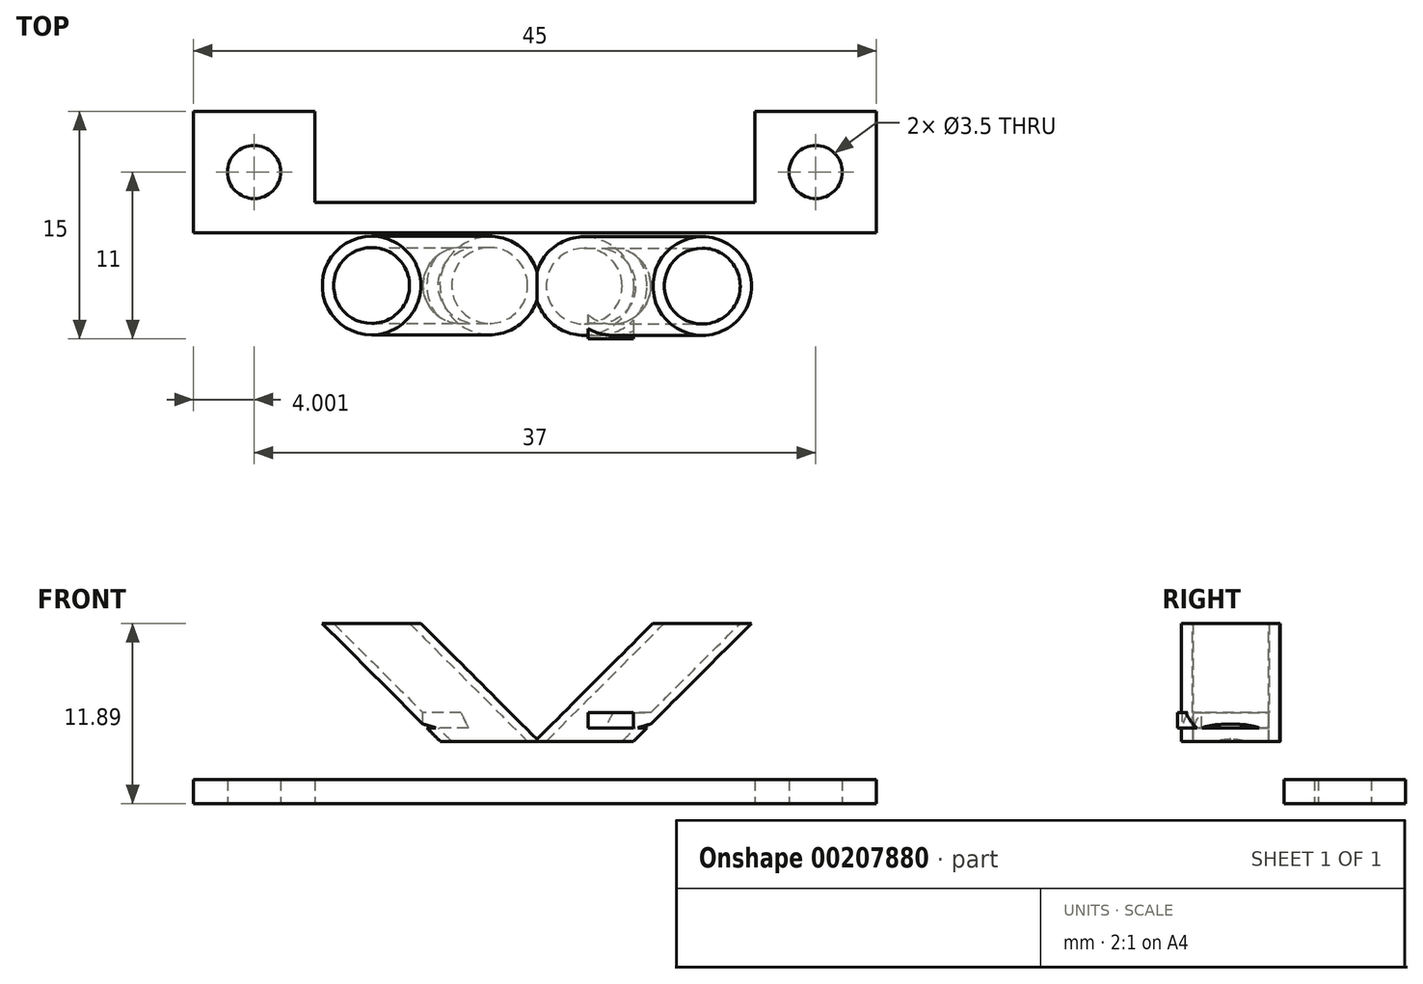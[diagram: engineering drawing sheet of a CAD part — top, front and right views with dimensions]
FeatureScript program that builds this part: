
annotation { "Feature Type Name" : "Feature", "Feature Type Description" : "" }
export const myFeature = defineFeature(function(context is Context, id is Id, definition is map)
    precondition{}
    {
        {
            var Q0;
            Q0=qCreatedBy(makeId("Top.planeOp"),FACE);
            var sketch = newSketch(context, id + "F0", { "sketchPlane" : qUnion([Q0])});
            skLineSegment(sketch, "E0.bottom", {"start": v(-20.07, 6) * mm, "end": v(-12.07, 6) * mm});
            skLineSegment(sketch, "E0.top", {"start": v(-20.07, -2) * mm, "end": v(-12.07, -2) * mm});
            skLineSegment(sketch, "E0.left", {"start": v(-20.07, 6) * mm, "end": v(-20.07, -2) * mm});
            skLineSegment(sketch, "E0.right", {"start": v(-12.07, 6) * mm, "end": v(-12.07, -2) * mm});
            skLineSegment(sketch, "E1.bottom", {"start": v(16.93, 6) * mm, "end": v(24.93, 6) * mm});
            skLineSegment(sketch, "E1.top", {"start": v(16.93, -2) * mm, "end": v(24.93, -2) * mm});
            skLineSegment(sketch, "E1.left", {"start": v(16.93, 6) * mm, "end": v(16.93, -2) * mm});
            skLineSegment(sketch, "E1.right", {"start": v(24.93, 6) * mm, "end": v(24.93, -2) * mm});
            skLineSegment(sketch, "E2.bottom", {"start": v(-12.07, 0) * mm, "end": v(16.93, 0) * mm});
            skLineSegment(sketch, "E2.top", {"start": v(-12.07, -2) * mm, "end": v(16.93, -2) * mm});
            skLineSegment(sketch, "E2.left", {"start": v(-12.07, 0) * mm, "end": v(-12.07, -2) * mm});
            skLineSegment(sketch, "E2.right", {"start": v(16.93, 0) * mm, "end": v(16.93, -2) * mm});
            skLineSegment(sketch, "E3.top", {"start": v(-12.07, -9) * mm, "end": v(16.93, -9) * mm});
            skLineSegment(sketch, "E3.left", {"start": v(-12.07, -2) * mm, "end": v(-12.07, -9) * mm});
            skLineSegment(sketch, "E3.right", {"start": v(16.93, -2) * mm, "end": v(16.93, -9) * mm});
            skLineSegment(sketch, "E4.bottom", {"start": v(-4.07, -9) * mm, "end": v(-1.07, -9) * mm});
            skLineSegment(sketch, "E4.top", {"start": v(-4.07, -5) * mm, "end": v(-1.07, -5) * mm});
            skLineSegment(sketch, "E4.left", {"start": v(-4.07, -9) * mm, "end": v(-4.07, -5) * mm});
            skLineSegment(sketch, "E4.right", {"start": v(-1.07, -9) * mm, "end": v(-1.07, -5) * mm});
            skLineSegment(sketch, "E5.bottom", {"start": v(5.93, -5) * mm, "end": v(8.93, -5) * mm});
            skLineSegment(sketch, "E5.top", {"start": v(5.93, -9) * mm, "end": v(8.93, -9) * mm});
            skLineSegment(sketch, "E5.left", {"start": v(5.93, -5) * mm, "end": v(5.93, -9) * mm});
            skLineSegment(sketch, "E5.right", {"start": v(8.93, -5) * mm, "end": v(8.93, -9) * mm});
            skCircle(sketch, "E6", {"center": v(20.93, 2) * mm, "radius": 1.75 * mm});
            skPoint(sketch, "E6.centerSnap0", {"position": v(16.93, 2) * mm});
            skPoint(sketch, "E6.centerSnap1", {"position": v(20.93, 6) * mm});
            skCircle(sketch, "E7", {"center": v(-16.07, 2) * mm, "radius": 1.75 * mm});
            skPoint(sketch, "E7.centerSnap0", {"position": v(-20.07, 2) * mm});
            skPoint(sketch, "E7.centerSnap1", {"position": v(-16.07, 6) * mm});
            skSolve(sketch);
        }
        {
            var Q0;
            Q0=makeQuery(id+"F0.imprint","IMPRINT",FACE,{"disambiguationData":[TD([[makeQuery(id+"F0.imprint","IMPRINT",EDGE,{"derivedFrom":sQuery(id+"F0.wireOp",EDGE,"E0.bottom")}),-1.0]])]});
            var Q1;
            Q1=makeQuery(id+"F0.imprint","IMPRINT",FACE,{"disambiguationData":[TD([[makeQuery(id+"F0.imprint","IMPRINT",EDGE,{"derivedFrom":sQuery(id+"F0.wireOp",EDGE,"E2.bottom")}),-1.0]])]});
            var Q2;
            Q2=makeQuery(id+"F0.imprint","IMPRINT",FACE,{"disambiguationData":[TD([[makeQuery(id+"F0.imprint","IMPRINT",EDGE,{"derivedFrom":sQuery(id+"F0.wireOp",EDGE,"E1.bottom")}),-1.0]])]});
            extrude(context, id + "F1", {"entities" : qUnion([Q0, Q1, Q2]), "depth" : 1.6 * mm});
        }
        {
            var Q0;
            Q0=makeQuery(id+"F0.imprint","IMPRINT",FACE,{"disambiguationData":[TD([[makeQuery(id+"F0.imprint","IMPRINT",EDGE,{"derivedFrom":sQuery(id+"F0.wireOp",EDGE,"E2.top")}),-1.0]])]});
            var Q1;
            Q1=makeQuery(id+"F0.imprint","IMPRINT",FACE,{"disambiguationData":[TD([[makeQuery(id+"F0.imprint","IMPRINT",EDGE,{"derivedFrom":sQuery(id+"F0.wireOp",EDGE,"E4.bottom")}),1.0]])]});
            var Q2;
            Q2=makeQuery(id+"F0.imprint","IMPRINT",FACE,{"disambiguationData":[TD([[makeQuery(id+"F0.imprint","IMPRINT",EDGE,{"derivedFrom":sQuery(id+"F0.wireOp",EDGE,"E5.bottom")}),-1.0]])]});
            extrude(context, id + "F2", {"entities" : qUnion([Q0, Q1, Q2]), "operationType" : NewBodyOperationType.ADD, "depth" : 6 * mm});
        }
        {
            var Q0;
            Q0=makeQuery(id+"F0.imprint","IMPRINT",FACE,{"disambiguationData":[TD([[makeQuery(id+"F0.imprint","IMPRINT",EDGE,{"derivedFrom":sQuery(id+"F0.wireOp",EDGE,"E4.bottom")}),1.0]])]});
            var Q1;
            Q1=makeQuery(id+"F0.imprint","IMPRINT",FACE,{"disambiguationData":[TD([[makeQuery(id+"F0.imprint","IMPRINT",EDGE,{"derivedFrom":sQuery(id+"F0.wireOp",EDGE,"E5.bottom")}),-1.0]])]});
            extrude(context, id + "F3", {"entities" : qUnion([Q0, Q1]), "operationType" : NewBodyOperationType.REMOVE, "depth" : 5 * mm});
        }
        {
            var Q0;
            Q0=makeQuery(id+"F2.opExtrude","CAP_FACE",FACE,{"disambiguationData":[OSD([sQuery(id+"F0.wireOp",EDGE,"E2.top"),sQuery(id+"F0.wireOp",EDGE,"E3.top"),sQuery(id+"F0.wireOp",EDGE,"E3.left"),sQuery(id+"F0.wireOp",EDGE,"E3.right"),sQuery(id+"F0.wireOp",EDGE,"E4.bottom"),sQuery(id+"F0.wireOp",EDGE,"E5.top")])],"isStart":false});
            var sketch = newSketch(context, id + "F4", { "sketchPlane" : qUnion([Q0])});
            skCircle(sketch, "E8", {"center": v(-2.44, -5.48) * mm, "radius": 2.5 * mm});
            skCircle(sketch, "E9", {"center": v(-2.44, -5.48) * mm, "radius": 3.25 * mm});
            skCircle(sketch, "E10", {"center": v(7.56, -5.52) * mm, "radius": 2.5 * mm});
            skCircle(sketch, "E11", {"center": v(7.56, -5.52) * mm, "radius": 3.25 * mm});
            skSolve(sketch);
        }
        {
            var Q0;
            Q0=qCreatedBy(makeId("Front.planeOp"),FACE);
            var sketch = newSketch(context, id + "F5", { "sketchPlane" : qUnion([Q0])});
            skLineSegment(sketch, "E12", {"start": v(-2.54, 4.11) * mm, "end": v(-10.32, 11.9) * mm});
            skLineSegment(sketch, "E13", {"start": v(-2.54, 4.11) * mm, "end": v(7.46, 4.11) * mm});
            skLineSegment(sketch, "E14", {"start": v(7.46, 4.11) * mm, "end": v(15.23, 11.9) * mm});
            skSolve(sketch);
        }
        {
            var Q0;
            Q0=makeQuery(id+"F4.imprint","IMPRINT",FACE,{"disambiguationData":[TD([[makeQuery(id+"F4.imprint","IMPRINT",EDGE,{"derivedFrom":sQuery(id+"F4.wireOp",EDGE,"E10")}),-1.0]])]});
            var Q1;
            Q1=sQuery(id+"F5.wireOp",EDGE,"E14");
            sweep(context, id + "F6", {"operationType" : NewBodyOperationType.ADD, "profiles" : qUnion([Q0]), "path" : qUnion([Q1])});
        }
        {
            var Q0;
            Q0=makeQuery(id+"F4.imprint","IMPRINT",FACE,{"disambiguationData":[TD([[makeQuery(id+"F4.imprint","IMPRINT",EDGE,{"derivedFrom":sQuery(id+"F4.wireOp",EDGE,"E8")}),-1.0]])]});
            var Q1;
            Q1=sQuery(id+"F5.wireOp",EDGE,"E12");
            sweep(context, id + "F7", {"operationType" : NewBodyOperationType.ADD, "profiles" : qUnion([Q0]), "path" : qUnion([Q1])});
        }
        {
            var Q0;
            Q0=makeQuery(id+"F4.imprint","IMPRINT",FACE,{"disambiguationData":[TD([[makeQuery(id+"F4.imprint","IMPRINT",EDGE,{"derivedFrom":sQuery(id+"F4.wireOp",EDGE,"E8")}),1.0]])]});
            var Q1;
            Q1=makeQuery(id+"F4.imprint","IMPRINT",FACE,{"disambiguationData":[TD([[makeQuery(id+"F4.imprint","IMPRINT",EDGE,{"derivedFrom":sQuery(id+"F4.wireOp",EDGE,"E10")}),1.0]])]});
            extrude(context, id + "F8", {"entities" : qUnion([Q0, Q1]), "operationType" : NewBodyOperationType.REMOVE, "oppositeDirection" : true, "depth" : 1 * mm});
        }
    });
